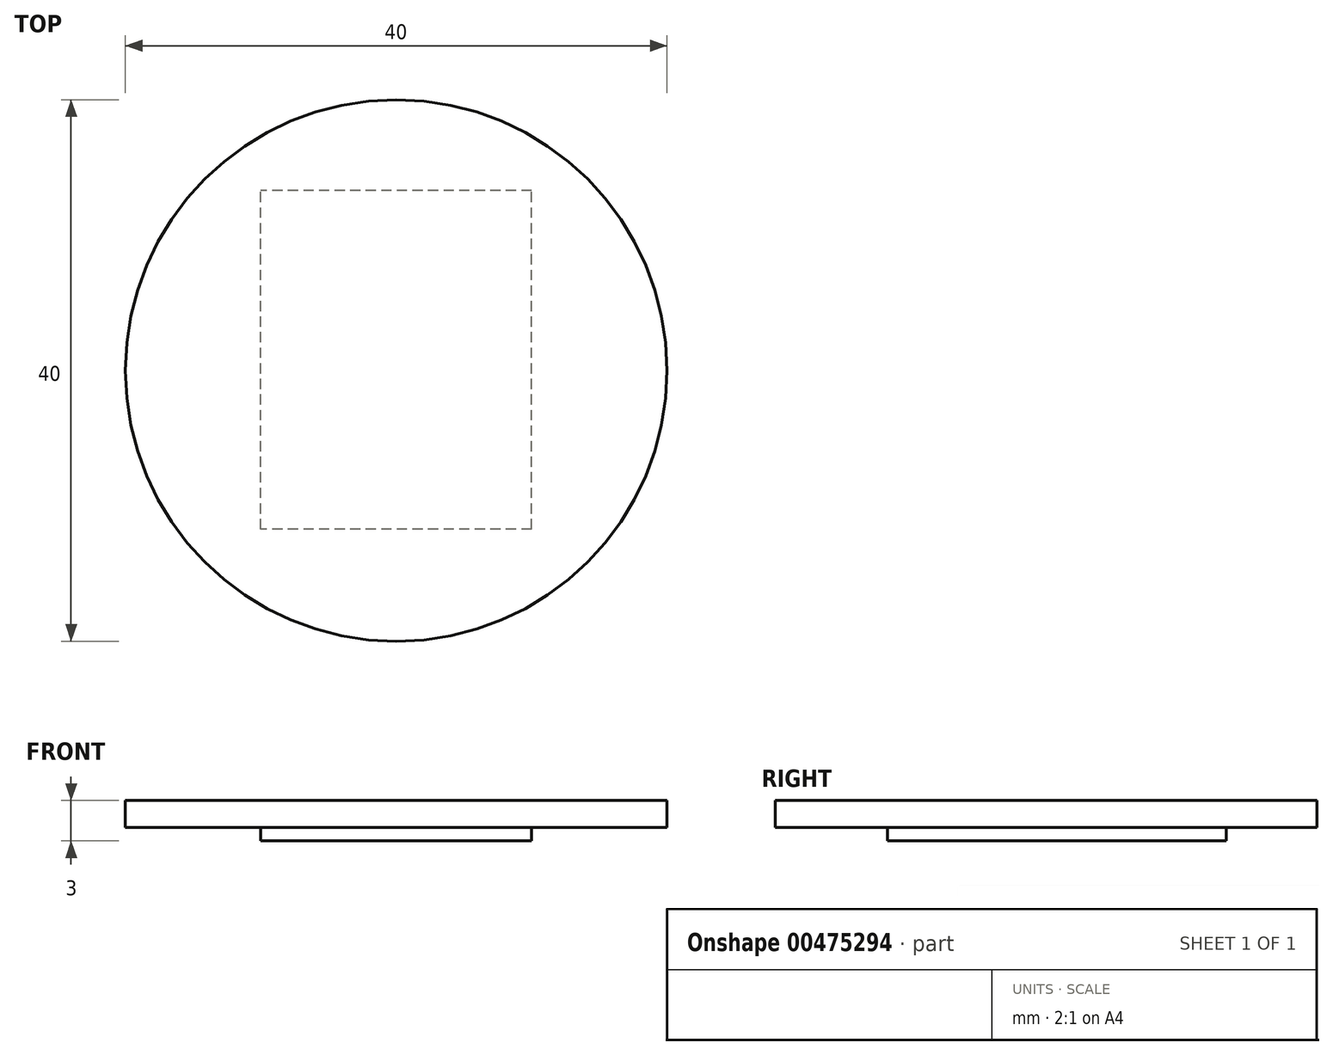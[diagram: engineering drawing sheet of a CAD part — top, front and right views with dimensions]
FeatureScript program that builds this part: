
annotation { "Feature Type Name" : "Feature", "Feature Type Description" : "" }
export const myFeature = defineFeature(function(context is Context, id is Id, definition is map)
    precondition{}
    {
        {
            var Q0;
            Q0=qCreatedBy(makeId("Top.planeOp"),FACE);
            var sketch = newSketch(context, id + "F0", { "sketchPlane" : qUnion([Q0])});
            skLineSegment(sketch, "E0.bottom", {"start": v(10, 12.5) * mm, "end": v(-10, 12.5) * mm});
            skLineSegment(sketch, "E0.top", {"start": v(10, -12.5) * mm, "end": v(-10, -12.5) * mm});
            skLineSegment(sketch, "E0.left", {"start": v(10, 12.5) * mm, "end": v(10, -12.5) * mm});
            skLineSegment(sketch, "E0.right", {"start": v(-10, 12.5) * mm, "end": v(-10, -12.5) * mm});
            skPoint(sketch, "E0.middle", {"position": v(0, 0) * mm});
            skCircle(sketch, "E1", {"center": v(0, 0) * mm, "radius": 20 * mm});
            skSolve(sketch);
        }
        {
            var Q0;
            Q0=makeQuery(id+"F0.imprint","IMPRINT",FACE,{"disambiguationData":[TD([[makeQuery(id+"F0.imprint","IMPRINT",EDGE,{"derivedFrom":sQuery(id+"F0.wireOp",EDGE,"E0.bottom")}),-1.0]])]});
            var Q1;
            Q1=makeQuery(id+"F0.imprint","IMPRINT",FACE,{"disambiguationData":[TD([[makeQuery(id+"F0.imprint","IMPRINT",EDGE,{"derivedFrom":sQuery(id+"F0.wireOp",EDGE,"E0.bottom")}),1.0]])]});
            extrude(context, id + "F1", {"entities" : qUnion([Q0, Q1]), "depth" : 2 * mm});
        }
        {
            var Q0;
            Q0=qCreatedBy(makeId("Top.planeOp"),FACE);
            var sketch = newSketch(context, id + "F2", { "sketchPlane" : qUnion([Q0])});
            skLineSegment(sketch, "E2.bottom", {"start": v(10, -11.71) * mm, "end": v(-10, -11.71) * mm});
            skLineSegment(sketch, "E2.top", {"start": v(10, 13.29) * mm, "end": v(-10, 13.29) * mm});
            skLineSegment(sketch, "E2.left", {"start": v(10, -11.71) * mm, "end": v(10, 13.29) * mm});
            skLineSegment(sketch, "E2.right", {"start": v(-10, -11.71) * mm, "end": v(-10, 13.29) * mm});
            skPoint(sketch, "E2.middle", {"position": v(0, 0.79) * mm});
            skSolve(sketch);
        }
        {
            var Q0;
            Q0=makeQuery(id+"F2.imprint","IMPRINT",FACE,{"disambiguationData":[TD([[makeQuery(id+"F2.imprint","IMPRINT",EDGE,{"derivedFrom":sQuery(id+"F2.wireOp",EDGE,"E2.bottom")}),-1.0]])]});
            extrude(context, id + "F3", {"entities" : qUnion([Q0]), "operationType" : NewBodyOperationType.ADD, "oppositeDirection" : true, "depth" : 1 * mm});
        }
    });
